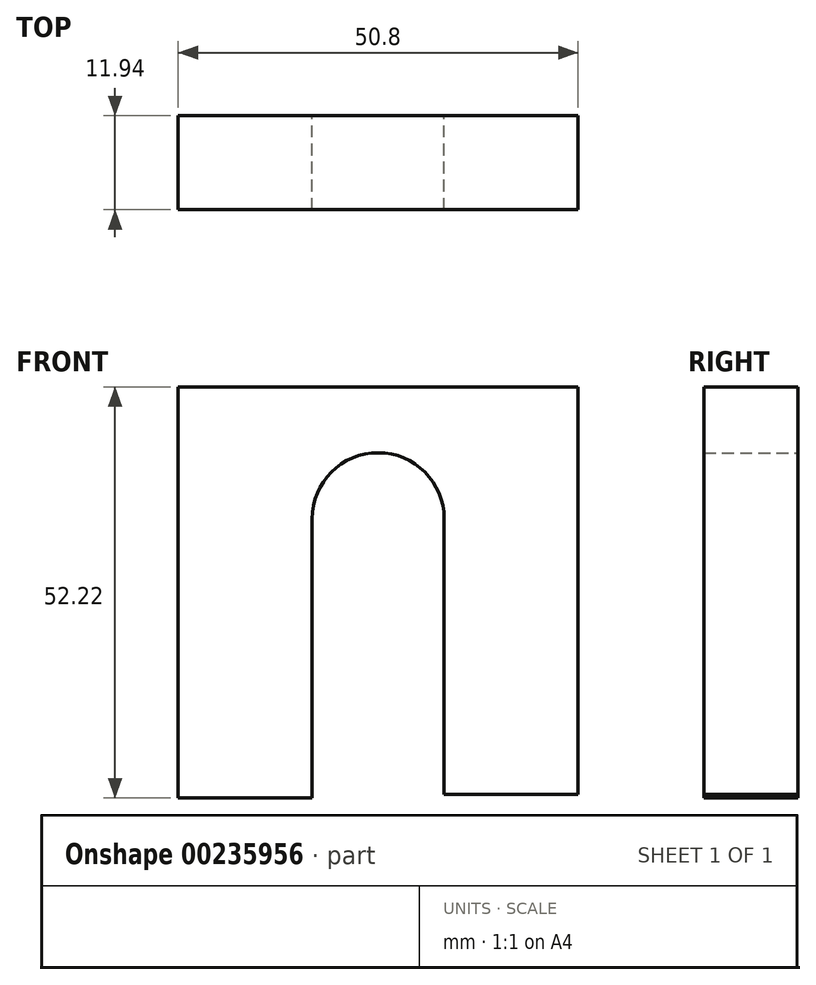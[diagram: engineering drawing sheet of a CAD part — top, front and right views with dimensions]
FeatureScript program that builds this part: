
annotation { "Feature Type Name" : "Feature", "Feature Type Description" : "" }
export const myFeature = defineFeature(function(context is Context, id is Id, definition is map)
    precondition{}
    {
        {
            var Q0;
            Q0=qCreatedBy(makeId("Front.planeOp"),FACE);
            var sketch = newSketch(context, id + "F0", { "sketchPlane" : qUnion([Q0])});
            skLineSegment(sketch, "E0", {"start": v(-24.57, 25.58) * mm, "end": v(26.23, 25.58) * mm});
            skLineSegment(sketch, "E1", {"start": v(26.23, 25.58) * mm, "end": v(26.23, -26.23) * mm});
            skLineSegment(sketch, "E2", {"start": v(-24.57, 25.58) * mm, "end": v(-24.57, -26.64) * mm});
            skLineSegment(sketch, "E3", {"start": v(-24.57, -26.64) * mm, "end": v(-7.55, -26.64) * mm});
            skLineSegment(sketch, "E4", {"start": v(26.23, -26.23) * mm, "end": v(9.22, -26.23) * mm});
            skLineSegment(sketch, "E5", {"start": v(0.83, 25.58) * mm, "end": v(0.83, 17.2) * mm});
            skPoint(sketch, "E5.endSnap0", {"position": v(0.83, 25.58) * mm});
            skCircle(sketch, "E6", {"center": v(0.83, 8.81) * mm, "radius": 8.38 * mm});
            skLineSegment(sketch, "E7", {"start": v(-7.55, -26.64) * mm, "end": v(-7.55, 8.81) * mm});
            skLineSegment(sketch, "E8", {"start": v(9.22, -26.23) * mm, "end": v(9.22, 8.81) * mm});
            skSolve(sketch);
        }
        {
            var Q0;
            {var subQ0=sQuery(id+"F0.wireOp",EDGE,"E1");Q0=makeQuery(id+"F0.imprint","IMPRINT",FACE,{"disambiguationData":[TD([[makeQuery(id+"F0.imprint","IMPRINT",EDGE,{"derivedFrom":subQ0}),-1.0]])]});}
            var Q1;
            {var subQ1=sQuery(id+"F0.wireOp",EDGE,"E2");Q1=makeQuery(id+"F0.imprint","IMPRINT",FACE,{"disambiguationData":[TD([[makeQuery(id+"F0.imprint","IMPRINT",EDGE,{"derivedFrom":subQ1}),1.0]])]});}
            extrude(context, id + "F1", {"entities" : qUnion([Q0, Q1]), "depth" : 11.94 * mm});
        }
    });
